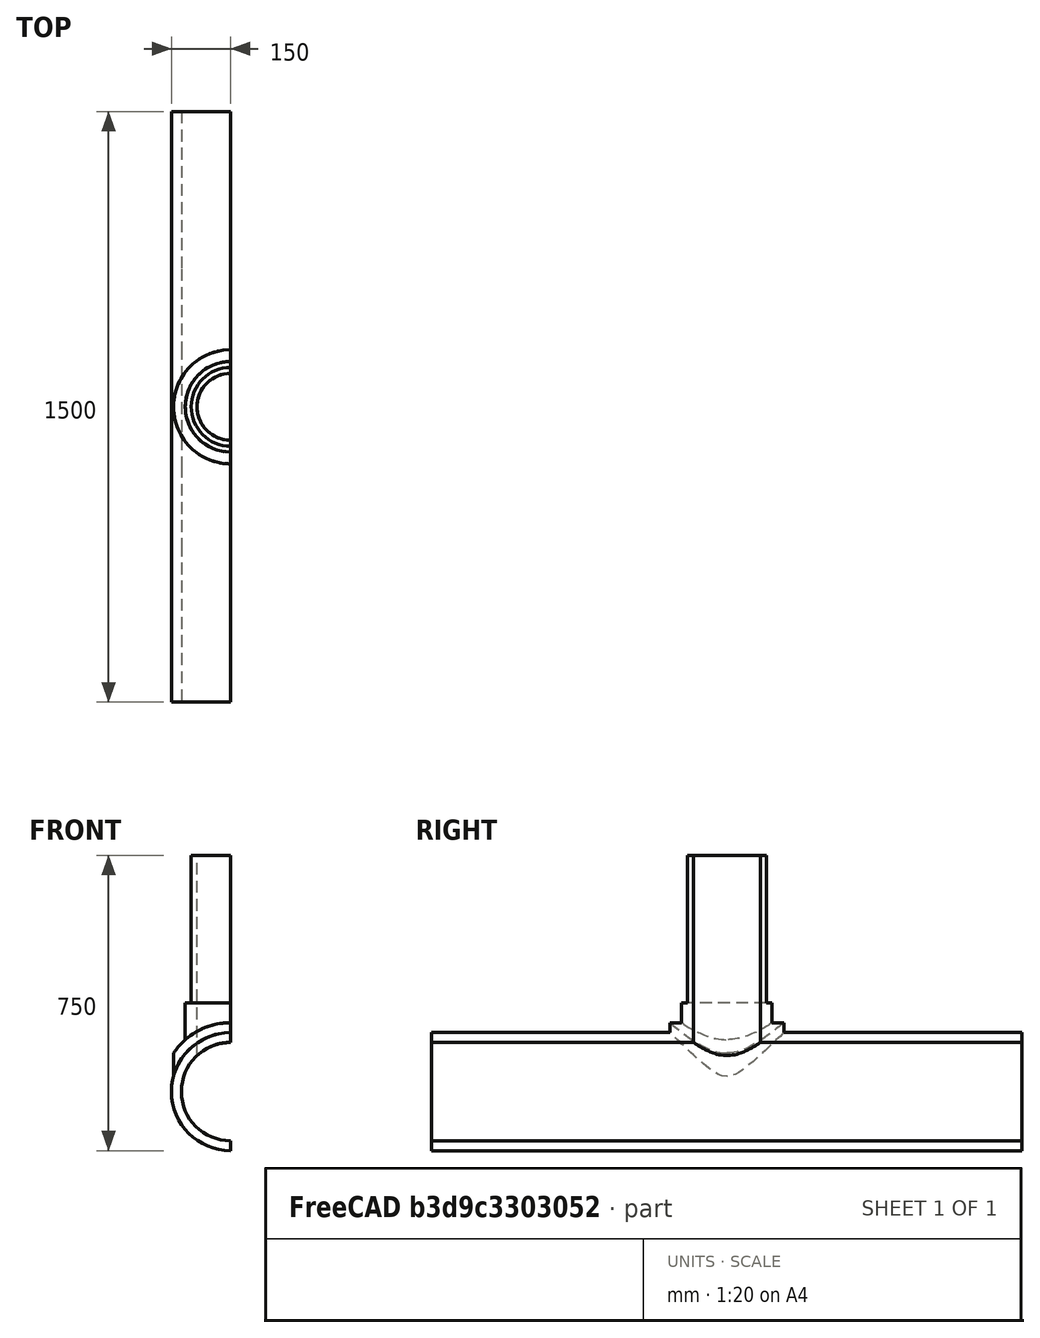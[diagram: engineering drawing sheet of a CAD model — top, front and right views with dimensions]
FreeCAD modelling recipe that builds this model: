
FCSTD DOCUMENT  (FreeCAD 0.16RUnknown)
Label: T-pipe transient thermo FEM model 1
License: All rights reserved
LicenseURL: http://en.wikipedia.org/wiki/All_rights_reserved
objects: Part::Cylinder×11, Part::Cut×8, Part::Box×3, Part::MultiFuse×3, Fem::ConstraintDisplacement×3, Fem::ConstraintHeatflux×2, Fem::ConstraintPressure×2, Fem::FemSolverObjectPython×1, Fem::FemMeshShapeNetgenObject×1, App::MaterialObjectPython×1, Fem::ConstraintInitialTemperature×1, Fem::FemAnalysisPython×1
note: 25 computed .brp shape members not serialized (recipe doc carries the construction recipe); baked Part::Feature solids carry a one-line shape summary decoded from their .brp

FEATURE [Part::Cylinder] Cylinder
  Angle = 360
  Height = 600
  Radius = 100
FEATURE [Part::Cylinder] Cylinder001
  Angle = 360
  Height = 1500
  Placement = pos=(0,750,0) rot=(1,0,0;1.5708rad)
  Radius = 150
FEATURE [Part::Cylinder] Cylinder002
  Angle = 360
  Height = 225
  Radius = 115
FEATURE [Part::Cylinder] Cylinder003
  Angle = 360
  Height = 400
  Placement = pos=(0,200,0) rot=(1,0,0;1.5708rad)
  Radius = 175
FEATURE [Part::Cylinder] Cylinder004
  Angle = 360
  Height = 600
  Radius = 145
FEATURE [Part::Cylinder] Cylinder005
  Angle = 360
  Height = 600
  Radius = 300
FEATURE [Part::Cut] Cut
  Base = -> Cylinder005
  Tool = -> Cylinder004
FEATURE [Part::Cut] Cut001
  Base = -> Cylinder003
  Tool = -> Cut
FEATURE [Part::Box] Box  label="Cube"
  Height = 500
  Length = 500
  Placement = pos=(-226,-279,-480) rot=(0,0,1;0rad)
  Width = 500
FEATURE [Part::Cut] Cut002
  Base = -> Cut001
  Tool = -> Box
FEATURE [Part::MultiFuse] Fusion
  Shapes = -> [Cut002,Cylinder002,Cylinder001,Cylinder]
FEATURE [Part::Cylinder] Cylinder006
  Angle = 360
  Height = 600
  Radius = 85
FEATURE [Part::Cut] Cut003
  Base = -> Fusion
  Tool = -> Cylinder006
FEATURE [Part::Cylinder] Cylinder007
  Angle = 360
  Height = 1500
  Placement = pos=(0,750,0) rot=(1,0,0;1.5708rad)
  Radius = 125
FEATURE [Part::Cut] Cut004
  Base = -> Cut003
  Tool = -> Cylinder007
FEATURE [Part::Box] Box001  label="Cube001"
  Height = 1000
  Length = 500
  Placement = pos=(0,-815,-274) rot=(0,0,1;0rad)
  Width = 1800
FEATURE [Part::Cut] Cut005
  Base = -> Cut004
  Tool = -> Box001
FEATURE [Part::Cylinder] Cylinder009
  Angle = 360
  Height = 200
  Placement = pos=(0,-150,0) rot=(1,0,0;1.5708rad)
  Radius = 150
FEATURE [Part::Cylinder] Cylinder010
  Angle = 360
  Height = 200
  Placement = pos=(0,350,0) rot=(1,0,0;1.5708rad)
  Radius = 150
FEATURE [Part::MultiFuse] Fusion002
  Shapes = -> [Cylinder009,Cylinder010]
FEATURE [Part::Cylinder] Cylinder011
  Angle = 360
  Height = 1500
  Placement = pos=(0,750,0) rot=(1,0,0;1.5708rad)
  Radius = 125
FEATURE [Part::MultiFuse] Fusion003
  Shapes = -> [Fusion002,Cut005]
FEATURE [Part::Box] Box002  label="Cube002"
  Height = 1000
  Length = 500
  Placement = pos=(0,-815,-274) rot=(0,0,1;0rad)
  Width = 1800
FEATURE [Part::Cut] Cut006
  Base = -> Fusion003
  Tool = -> Cylinder011
FEATURE [Part::Cut] Cut007
  Base = -> Cut006
  Tool = -> Box002
FEATURE [Fem::FemSolverObjectPython] CalculiX  # FEM object (typed FeaturePython)
  AnalysisType = 2
  EigenmodeHighLimit = 1000000
  EigenmodeLowLimit = 0
  EndTime = 5000
  InitialTimeStep = 15
  MatrixSolverType = 0
  Maxiterations = 2000
  NonLinearGeometry = false
  NumCpus = 4
  NumberOfEigenmodes = 10
  SolverType = FemSolverCalculix
  SteadyState = false
FEATURE [Fem::FemMeshShapeNetgenObject] Cut007_Mesh
  Fineness = 2
  GrowthRate = 0.3
  MaxSize = 1000
  NbSegsPerEdge = 1
  NbSegsPerRadius = 2
  Optimize = true
  SecondOrder = true
  Shape = -> Cut007
FEATURE [App::MaterialObjectPython] MechanicalMaterial  # material (typed FeaturePython)
  Material = Density=7900.0 kg/m^3,+10 more (map truncated)
FEATURE [Fem::ConstraintDisplacement] FemConstraintDisplacement
  NormalDirection = (1,0,0)
  Normals = (147) [(1,0,0),(1,0,0),(1,0,0),(1,0,0),(1,0,0),(1,0,0),(1,0,0),(1,0,0),(1,0,0),(1,0,0),(1,0,0),(1,0,0),(1,0,0),(1,0,0),(1,0,0),(1,0,0),(1,0,0),(1,0,0),+129 more]
  Points = (147) [(0,-85,125),(0,-150,125),(0,-150,133.333),(0,-150,141.667),(0,-150,150),(0,-216.667,125),(0,-216.667,133.333),(0,-216.667,141.667),(0,-216.667,150),+138 more]
  References = -> [Cut007]
  rotxFix = false
  rotxFree = true
  rotyFix = false
  rotyFree = true
  rotzFix = false
  rotzFree = true
  xDisplacement = 0
  xFix = true
  xFree = false
  xRotation = 0
  yDisplacement = 0
  yFix = false
  yFree = true
  yRotation = 0
  zDisplacement = 0
  zFix = false
  zFree = true
  zRotation = 0
FEATURE [Fem::ConstraintDisplacement] FemConstraintDisplacement001
  NormalDirection = (0,-1,0)
  Normals = (2) [(0,-1,2.22045e-16),(0,-1,2.22045e-16)]
  Points = (2) [(0,-750,-150),(0,-750,150)]
  References = -> [Cut007]
  Scale = 16
  rotxFix = false
  rotxFree = true
  rotyFix = false
  rotyFree = true
  rotzFix = false
  rotzFree = true
  xDisplacement = 0
  xFix = false
  xFree = true
  xRotation = 0
  yDisplacement = 0
  yFix = true
  yFree = false
  yRotation = 0
  zDisplacement = 0
  zFix = false
  zFree = true
  zRotation = 0
FEATURE [Fem::ConstraintDisplacement] FemConstraintDisplacement002
  NormalDirection = (0,0,1)
  Normals = (2) [(0,0,1),(0,0,1)]
  Points = (2) [(0,-100,600),(0,100,600)]
  References = -> [Cut007]
  Scale = 13
  rotxFix = false
  rotxFree = true
  rotyFix = false
  rotyFree = true
  rotzFix = false
  rotzFree = true
  xDisplacement = 0
  xFix = false
  xFree = true
  xRotation = 0
  yDisplacement = 0
  yFix = false
  yFree = true
  yRotation = 0
  zDisplacement = 0
  zFix = true
  zFree = false
  zRotation = 0
FEATURE [Fem::ConstraintHeatflux] FemConstraintHeatflux
  AmbientTemp = 725
  FilmCoef = 1000
  NormalDirection = (1,0,0)
  Normals = (90) [(-6.12323e-17,-2.22045e-16,-1),(0.866025,-1.11022e-16,-0.5),(0.866025,1.11022e-16,0.5),(1.83697e-16,2.22045e-16,1),(-6.12323e-17,-2.22045e-16,-1),+85 more]
  Points = (90) [(7.65404e-15,-350,125),(-108.253,-350,62.5),(-108.253,-350,-62.5),(-2.29621e-14,-350,-125),(7.65404e-15,-483.333,125),(-108.253,-483.333,62.5),+84 more]
  References = -> [Cut007]
  Scale = 21
FEATURE [Fem::ConstraintHeatflux] FemConstraintHeatflux001
  AmbientTemp = 300
  FilmCoef = 10
  NormalDirection = (-1,0,2.0353e-08)
  Normals = (32) [(4.07057e-08,2.22045e-16,1),(-0.866025,1.11022e-16,0.5),(-0.866025,-1.11022e-16,-0.5),(-1.83697e-16,-2.22045e-16,-1),(-0.866025,-1.11022e-16,-0.5),+27 more]
  Points = (32) [(6.10585e-06,150,150),(-129.904,150,75),(-129.904,150,-75),(-2.75546e-14,150,-150),(-129.904,50,-75),(-2.75546e-14,50,-150),(-129.904,-50,-75),+25 more]
  References = -> [Cut007]
  Scale = 14
FEATURE [Fem::ConstraintPressure] FemConstraintPressure
  NormalDirection = (1,0,0)
  Normals = (90) [(-6.12323e-17,-2.22045e-16,-1),(0.866025,-1.11022e-16,-0.5),(0.866025,1.11022e-16,0.5),(1.83697e-16,2.22045e-16,1),(-6.12323e-17,-2.22045e-16,-1),+85 more]
  Points = (90) [(7.65404e-15,-350,125),(-108.253,-350,62.5),(-108.253,-350,-62.5),(-2.29621e-14,-350,-125),(7.65404e-15,-483.333,125),(-108.253,-483.333,62.5),+84 more]
  Pressure = 9
  References = -> [Cut007]
  Scale = 21
FEATURE [Fem::ConstraintPressure] FemConstraintPressure001
  NormalDirection = (0,1,0)
  Normals = (2) [(0,1,-2.22045e-16),(0,1,-2.22045e-16)]
  Points = (2) [(0,750,-150),(0,750,150)]
  Pressure = 24.75
  References = -> [Cut007]
  Reversed = true
  Scale = 16
FEATURE [Fem::ConstraintInitialTemperature] FemConstraintInitialTemperature
  NormalDirection = (0,0,1)
  initialTemperature = 300
FEATURE [Fem::FemAnalysisPython] MechanicalAnalysis  # FEM object (typed FeaturePython)
  Member = -> [CalculiX,Cut007_Mesh,MechanicalMaterial,FemConstraintDisplacement,FemConstraintDisplacement001,FemConstraintDisplacement002,FemConstraintHeatflux,FemConstraintHeatflux001,FemConstraintPressure,FemConstraintPressure001,FemConstraintInitialTemperature]
